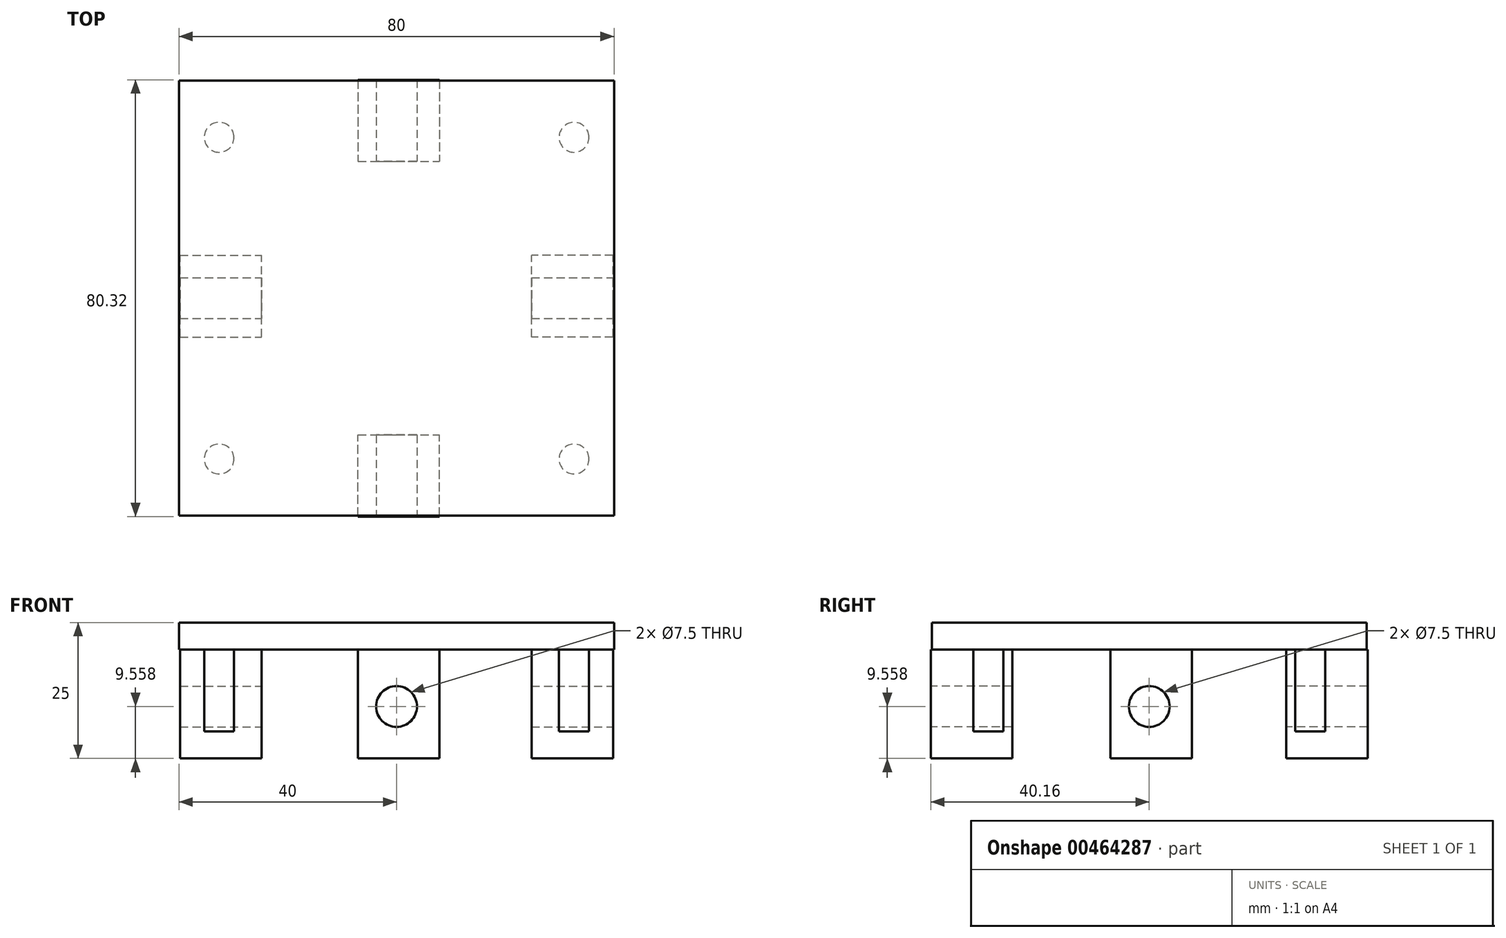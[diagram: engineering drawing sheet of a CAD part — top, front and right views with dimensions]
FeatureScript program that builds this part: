
annotation { "Feature Type Name" : "Feature", "Feature Type Description" : "" }
export const myFeature = defineFeature(function(context is Context, id is Id, definition is map)
    precondition{}
    {
        {
            var Q0;
            Q0=qCreatedBy(makeId("Top.planeOp"),FACE);
            var sketch = newSketch(context, id + "F0", { "sketchPlane" : qUnion([Q0])});
            skLineSegment(sketch, "E0.bottom", {"start": v(40, -40) * mm, "end": v(-40, -40) * mm});
            skLineSegment(sketch, "E0.top", {"start": v(40, 40) * mm, "end": v(-40, 40) * mm});
            skLineSegment(sketch, "E0.left", {"start": v(40, -40) * mm, "end": v(40, 40) * mm});
            skLineSegment(sketch, "E0.right", {"start": v(-40, -40) * mm, "end": v(-40, 40) * mm});
            skPoint(sketch, "E0.middle", {"position": v(0, 0) * mm});
            skSolve(sketch);
        }
        {
            var Q0;
            Q0=qSketchRegion(id+"F0",true);
            extrude(context, id + "F1", {"entities" : qUnion([Q0]), "depth" : 5 * mm});
        }
        {
            var Q0;
            Q0=qCreatedBy(makeId("Top.planeOp"),FACE);
            var sketch = newSketch(context, id + "F2", { "sketchPlane" : qUnion([Q0])});
            skLineSegment(sketch, "E1.bottom", {"start": v(-37.29, 40.06) * mm, "end": v(-22.29, 40.06) * mm, "construction": true});
            skLineSegment(sketch, "E1.top", {"start": v(-37.29, 25.06) * mm, "end": v(-22.29, 25.06) * mm, "construction": true});
            skLineSegment(sketch, "E1.left", {"start": v(-37.29, 40.06) * mm, "end": v(-37.29, 25.06) * mm, "construction": true});
            skLineSegment(sketch, "E1.right", {"start": v(-22.29, 40.06) * mm, "end": v(-22.29, 25.06) * mm, "construction": true});
            skLineSegment(sketch, "E2.MirrorCS", {"start": v(37.29, 25.06) * mm, "end": v(22.29, 25.06) * mm, "construction": true});
            skLineSegment(sketch, "E3.MirrorCS", {"start": v(22.29, 40.06) * mm, "end": v(22.29, 25.06) * mm, "construction": true});
            skLineSegment(sketch, "E4.MirrorCS", {"start": v(37.29, 40.06) * mm, "end": v(22.29, 40.06) * mm, "construction": true});
            skLineSegment(sketch, "E5.MirrorCS", {"start": v(37.29, 40.06) * mm, "end": v(37.29, 25.06) * mm, "construction": true});
            skLineSegment(sketch, "E6.MirrorCS", {"start": v(-37.29, -25.06) * mm, "end": v(-22.29, -25.06) * mm, "construction": true});
            skLineSegment(sketch, "E7.MirrorCS", {"start": v(-22.29, -40.06) * mm, "end": v(-22.29, -25.06) * mm, "construction": true});
            skLineSegment(sketch, "E8.MirrorCS", {"start": v(-37.29, -40.06) * mm, "end": v(-22.29, -40.06) * mm, "construction": true});
            skLineSegment(sketch, "E9.MirrorCS", {"start": v(-37.29, -40.06) * mm, "end": v(-37.29, -25.06) * mm, "construction": true});
            skLineSegment(sketch, "E10.MirrorCS", {"start": v(37.29, -25.06) * mm, "end": v(22.29, -25.06) * mm, "construction": true});
            skLineSegment(sketch, "E11.MirrorCS", {"start": v(22.29, -40.06) * mm, "end": v(22.29, -25.06) * mm, "construction": true});
            skLineSegment(sketch, "E12.MirrorCS", {"start": v(37.29, -40.06) * mm, "end": v(22.29, -40.06) * mm, "construction": true});
            skLineSegment(sketch, "E13.MirrorCS", {"start": v(37.29, -40.06) * mm, "end": v(37.29, -25.06) * mm, "construction": true});
            skLineSegment(sketch, "E14.MirrorCS", {"start": v(21, 25.03) * mm, "end": v(21, 40.03) * mm});
            skLineSegment(sketch, "E15.MirrorCS", {"start": v(-39.82, 7.86) * mm, "end": v(-24.82, 7.86) * mm});
            skLineSegment(sketch, "E16.MirrorCS", {"start": v(-24.82, -7.14) * mm, "end": v(-24.82, 7.86) * mm});
            skLineSegment(sketch, "E17.MirrorCS", {"start": v(-39.82, -7.14) * mm, "end": v(-24.82, -7.14) * mm});
            skLineSegment(sketch, "E18.MirrorCS", {"start": v(-39.82, -7.14) * mm, "end": v(-39.82, 7.86) * mm});
            skLineSegment(sketch, "E19.MirrorCS", {"start": v(39.82, -7.14) * mm, "end": v(24.82, -7.14) * mm});
            skLineSegment(sketch, "E20.MirrorCS", {"start": v(24.82, -7.14) * mm, "end": v(24.82, 7.86) * mm});
            skLineSegment(sketch, "E21.MirrorCS", {"start": v(39.82, 7.86) * mm, "end": v(24.82, 7.86) * mm});
            skLineSegment(sketch, "E22.MirrorCS", {"start": v(39.82, -7.14) * mm, "end": v(39.82, 7.86) * mm});
            skLineSegment(sketch, "E23.MirrorCS", {"start": v(-7.1, -25.16) * mm, "end": v(7.9, -25.16) * mm});
            skLineSegment(sketch, "E24.MirrorCS", {"start": v(7.9, -40.16) * mm, "end": v(7.9, -25.16) * mm});
            skLineSegment(sketch, "E25.MirrorCS", {"start": v(-7.1, -40.16) * mm, "end": v(7.9, -40.16) * mm});
            skLineSegment(sketch, "E26.MirrorCS", {"start": v(-7.1, -40.16) * mm, "end": v(-7.1, -25.16) * mm});
            skLineSegment(sketch, "E27.MirrorCS", {"start": v(-7.1, 25.16) * mm, "end": v(7.9, 25.16) * mm});
            skLineSegment(sketch, "E28.MirrorCS", {"start": v(-7.1, 40.16) * mm, "end": v(-7.1, 25.16) * mm});
            skLineSegment(sketch, "E29.MirrorCS", {"start": v(-7.1, 40.16) * mm, "end": v(7.9, 40.16) * mm});
            skLineSegment(sketch, "E30.MirrorCS", {"start": v(7.9, 40.16) * mm, "end": v(7.9, 25.16) * mm});
            skSolve(sketch);
        }
        {
            var Q0;
            Q0=qSketchRegion(id+"F2",true);
            var Q1;
            Q1=qConstructionFilter(qBodyType(qCreatedBy(id+"F2",EDGE),BodyType.WIRE),ConstructionObject.NO);
            extrude(context, id + "F3", {"entities" : qUnion([Q0]), "operationType" : NewBodyOperationType.ADD, "surfaceEntities" : qUnion([Q1]), "oppositeDirection" : true, "depth" : 20 * mm});
        }
        {
            var Q0;
            Q0=qCreatedBy(makeId("Front.planeOp"),FACE);
            cPlane(context, id + "F4", {"entities" : qUnion([Q0]), "cplaneType" : CPlaneType.OFFSET, "offset" : 41.1 * mm, "width" : 150 * mm, "height" : 150 * mm});
        }
        {
            var Q0;
            Q0=qCreatedBy(id+"F4.planeOp",FACE);
            var sketch = newSketch(context, id + "F5", { "sketchPlane" : qUnion([Q0])});
            skPoint(sketch, "E31", {"position": v(0, -10.44) * mm});
            skSolve(sketch);
        }
        {
            var Q0;
            Q0=sQuery(id+"F5.wireOp",VERTEX,"E31");
            var Q1;
            Q1=makeQuery(id+"F1.opExtrude","SWEPT_BODY",BODY,{"disambiguationData":[OSD([sQuery(id+"F0.wireOp",EDGE,"E0.bottom"),sQuery(id+"F0.wireOp",EDGE,"E0.top"),sQuery(id+"F0.wireOp",EDGE,"E0.left"),sQuery(id+"F0.wireOp",EDGE,"E0.right")])]});
            hole(context, id + "F6", {"style" : HoleStyle.SIMPLE, "endStyle" : HoleEndStyle.THROUGH, "holeDiameter" : 7.5 * mm, "isTappedThrough" : true, "tappedDepth" : 12 * mm, "tapClearance" : 3, "locations" : qUnion([Q0]), "scope" : qUnion([Q1])});
        }
        {
            var Q0;
            Q0=qCreatedBy(makeId("Right.planeOp"),FACE);
            cPlane(context, id + "F7", {"entities" : qUnion([Q0]), "cplaneType" : CPlaneType.OFFSET, "offset" : 59.3 * mm, "width" : 150 * mm, "height" : 150 * mm});
        }
        {
            var Q0;
            Q0=qCreatedBy(id+"F7.planeOp",FACE);
            var sketch = newSketch(context, id + "F8", { "sketchPlane" : qUnion([Q0])});
            skPoint(sketch, "E32", {"position": v(0, -10.44) * mm});
            skSolve(sketch);
        }
        {
            var Q0;
            Q0=sQuery(id+"F8.wireOp",VERTEX,"E32");
            var Q1;
            Q1=makeQuery(id+"F1.opExtrude","SWEPT_BODY",BODY,{"disambiguationData":[OSD([sQuery(id+"F0.wireOp",EDGE,"E0.bottom"),sQuery(id+"F0.wireOp",EDGE,"E0.top"),sQuery(id+"F0.wireOp",EDGE,"E0.left"),sQuery(id+"F0.wireOp",EDGE,"E0.right")])]});
            hole(context, id + "F9", {"style" : HoleStyle.SIMPLE, "endStyle" : HoleEndStyle.THROUGH, "holeDiameter" : 7.5 * mm, "isTappedThrough" : true, "tappedDepth" : 12 * mm, "tapClearance" : 3, "locations" : qUnion([Q0]), "scope" : qUnion([Q1])});
        }
        {
            var Q0;
            Q0=qCreatedBy(makeId("Top.planeOp"),FACE);
            var sketch = newSketch(context, id + "F10", { "sketchPlane" : qUnion([Q0])});
            skLineSegment(sketch, "E33.bottom", {"start": v(-40.13, 29.59) * mm, "end": v(-32.63, 29.59) * mm, "construction": true});
            skLineSegment(sketch, "E33.top", {"start": v(-40.13, 37.09) * mm, "end": v(-32.63, 37.09) * mm, "construction": true});
            skLineSegment(sketch, "E33.left", {"start": v(-40.13, 29.59) * mm, "end": v(-40.13, 37.09) * mm, "construction": true});
            skLineSegment(sketch, "E33.right", {"start": v(-32.63, 29.59) * mm, "end": v(-32.63, 37.09) * mm, "construction": true});
            skLineSegment(sketch, "E34", {"start": v(-40.13, 29.59) * mm, "end": v(-32.63, 37.09) * mm, "construction": true});
            skLineSegment(sketch, "E35", {"start": v(-32.63, 29.59) * mm, "end": v(-40.13, 37.09) * mm, "construction": true});
            skCircle(sketch, "E36", {"center": v(-32.63, 29.59) * mm, "radius": 2.75 * mm});
            skCircle(sketch, "E37.MirrorC", {"center": v(32.63, 29.59) * mm, "radius": 2.75 * mm});
            skCircle(sketch, "E38.MirrorC", {"center": v(32.63, -29.59) * mm, "radius": 2.75 * mm});
            skCircle(sketch, "E39.MirrorC", {"center": v(-32.63, -29.59) * mm, "radius": 2.75 * mm});
            skSolve(sketch);
        }
        {
            var Q0;
            Q0=qSketchRegion(id+"F10",true);
            extrude(context, id + "F11", {"entities" : qUnion([Q0]), "operationType" : NewBodyOperationType.ADD, "oppositeDirection" : true, "depth" : 15 * mm});
        }
    });
